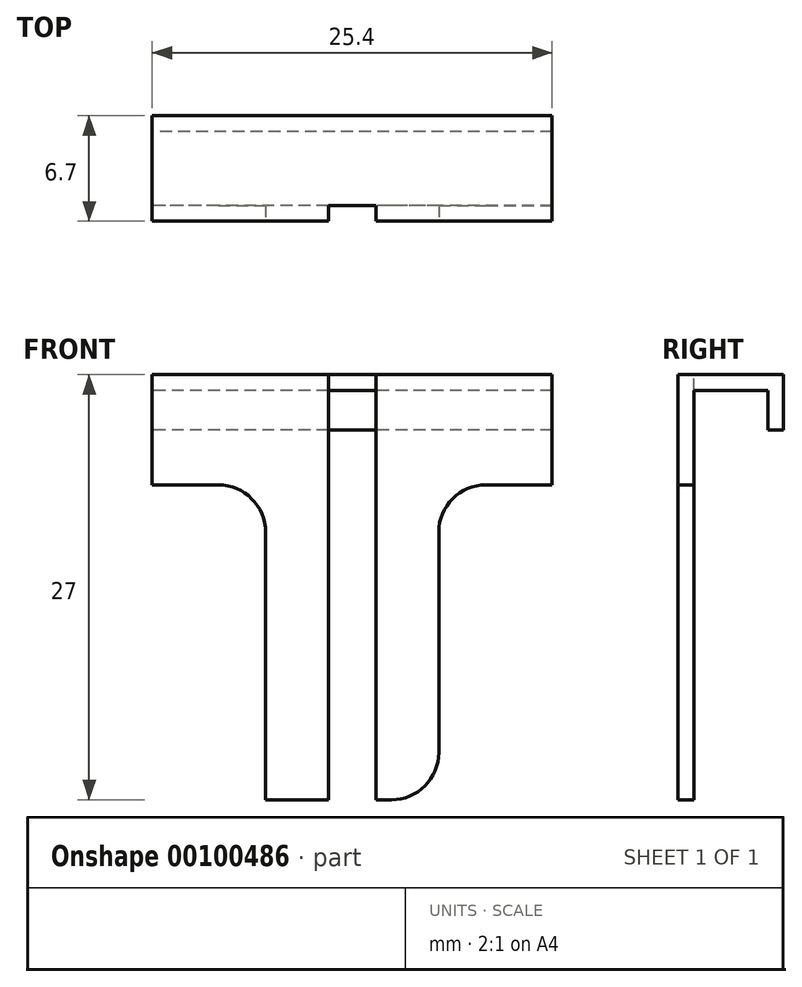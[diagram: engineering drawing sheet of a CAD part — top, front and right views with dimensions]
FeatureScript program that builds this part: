
annotation { "Feature Type Name" : "Feature", "Feature Type Description" : "" }
export const myFeature = defineFeature(function(context is Context, id is Id, definition is map)
    precondition{}
    {
        {
            var Q0;
            Q0=qCreatedBy(makeId("Right.planeOp"),FACE);
            var sketch = newSketch(context, id + "F0", { "sketchPlane" : qUnion([Q0])});
            skLineSegment(sketch, "E0", {"start": v(0, 0) * mm, "end": v(6.7, 0) * mm});
            skLineSegment(sketch, "E1", {"start": v(6.7, 0) * mm, "end": v(6.7, -3.5) * mm});
            skLineSegment(sketch, "E2", {"start": v(6.7, -3.5) * mm, "end": v(5.7, -3.5) * mm});
            skLineSegment(sketch, "E3", {"start": v(5.7, -3.5) * mm, "end": v(5.7, -1) * mm});
            skLineSegment(sketch, "E4", {"start": v(5.7, -1) * mm, "end": v(1, -1) * mm});
            skLineSegment(sketch, "E5", {"start": v(1, -1) * mm, "end": v(1, -27) * mm});
            skLineSegment(sketch, "E6", {"start": v(1, -27) * mm, "end": v(0, -27) * mm});
            skLineSegment(sketch, "E7", {"start": v(0, -27) * mm, "end": v(0, 0) * mm});
            skSolve(sketch);
        }
        {
            var Q0;
            Q0=qSketchRegion(id+"F0",true);
            extrude(context, id + "F1", {"entities" : qUnion([Q0]), "endBound" : BoundingType.SYMMETRIC, "depth" : 25.4 * mm});
        }
        {
            var Q0;
            Q0=makeQuery(id+"F1.opExtrude","SWEPT_FACE",FACE,{"disambiguationData":[OSD([sQuery(id+"F0.wireOp",EDGE,"E7")])]});
            var sketch = newSketch(context, id + "F2", { "sketchPlane" : qUnion([Q0])});
            skLineSegment(sketch, "E8", {"start": v(1.5, 0) * mm, "end": v(-1.5, 0) * mm});
            skLineSegment(sketch, "E9", {"start": v(-5.5, -27) * mm, "end": v(-5.5, -7) * mm});
            skLineSegment(sketch, "E10", {"start": v(5.5, -27) * mm, "end": v(5.5, -7) * mm});
            skLineSegment(sketch, "E11", {"start": v(5.5, -7) * mm, "end": v(12.7, -7) * mm});
            skLineSegment(sketch, "E12", {"start": v(-5.5, -7) * mm, "end": v(-12.7, -7) * mm});
            skLineSegment(sketch, "E13", {"start": v(-12.7, -7) * mm, "end": v(-12.7, -27) * mm});
            skLineSegment(sketch, "E14", {"start": v(-12.7, -27) * mm, "end": v(-5.5, -27) * mm});
            skLineSegment(sketch, "E15", {"start": v(5.5, -27) * mm, "end": v(12.7, -27) * mm});
            skLineSegment(sketch, "E16", {"start": v(12.7, -27) * mm, "end": v(12.7, -7) * mm});
            skLineSegment(sketch, "E17", {"start": v(1.5, -27) * mm, "end": v(1.5, 0) * mm});
            skLineSegment(sketch, "E18", {"start": v(-1.5, -27) * mm, "end": v(-1.5, 0) * mm});
            skLineSegment(sketch, "E19", {"start": v(-1.5, -27) * mm, "end": v(1.5, -27) * mm});
            skSolve(sketch);
        }
        {
            var Q0;
            Q0=qSketchRegion(id+"F2",true);
            var Q1;
            Q1=makeQuery(id+"F1.opExtrude","SWEPT_FACE",FACE,{"disambiguationData":[OSD([sQuery(id+"F0.wireOp",EDGE,"E5")])]});
            extrude(context, id + "F3", {"entities" : qUnion([Q0]), "operationType" : NewBodyOperationType.REMOVE, "endBound" : BoundingType.UP_TO_SURFACE, "oppositeDirection" : true, "endBoundEntityFace" : qUnion([Q1]), "depth" : 25 * mm});
        }
        {
            var Q0;
            Q0=makeQuery(id+"F3.boolean.opBoolean","COPY",EDGE,{"derivedFrom":makeQuery(id+"F3.opExtrude","SWEPT_EDGE",EDGE,{"disambiguationData":[OSD([sQuery(id+"F0.wireOp",EDGE,"E6"),sQuery(id+"F0.wireOp",EDGE,"E7"),sQuery(id+"F2.wireOp",EDGE,"E10"),sQuery(id+"F2.wireOp",EDGE,"E15")])]})});
            var Q1;
            Q1=makeQuery(id+"F3.boolean.opBoolean","COPY",EDGE,{"derivedFrom":makeQuery(id+"F3.opExtrude","SWEPT_EDGE",EDGE,{"disambiguationData":[OSD([sQuery(id+"F0.wireOp",EDGE,"E6"),sQuery(id+"F0.wireOp",EDGE,"E7"),sQuery(id+"F2.wireOp",EDGE,"E9"),sQuery(id+"F2.wireOp",EDGE,"E14")])]})});
            var Q2;
            Q2=makeQuery(id+"F3.boolean.opBoolean","COPY",EDGE,{"derivedFrom":makeQuery(id+"F3.opExtrude","SWEPT_EDGE",EDGE,{"disambiguationData":[OSD([sQuery(id+"F2.wireOp",EDGE,"E9"),sQuery(id+"F2.wireOp",EDGE,"E12")])]})});
            var Q3;
            Q3=makeQuery(id+"F3.boolean.opBoolean","COPY",EDGE,{"derivedFrom":makeQuery(id+"F3.opExtrude","SWEPT_EDGE",EDGE,{"disambiguationData":[OSD([sQuery(id+"F0.wireOp",EDGE,"E7"),sQuery(id+"F2.wireOp",EDGE,"E12"),sQuery(id+"F2.wireOp",EDGE,"E13")])]})});
            var Q4;
            Q4=makeQuery(id+"F3.boolean.opBoolean","COPY",EDGE,{"derivedFrom":makeQuery(id+"F3.opExtrude","SWEPT_EDGE",EDGE,{"disambiguationData":[OSD([sQuery(id+"F2.wireOp",EDGE,"E10"),sQuery(id+"F2.wireOp",EDGE,"E11")])]})});
            var Q5;
            Q5=makeQuery(id+"F3.boolean.opBoolean","COPY",EDGE,{"derivedFrom":makeQuery(id+"F3.opExtrude","SWEPT_EDGE",EDGE,{"disambiguationData":[OSD([sQuery(id+"F0.wireOp",EDGE,"E7"),sQuery(id+"F2.wireOp",EDGE,"E11"),sQuery(id+"F2.wireOp",EDGE,"E16")])]})});
            fillet(context, id + "F4", {"entities" : qUnion([Q0, Q1, Q2, Q3, Q4, Q5]), "radius" : 3 * mm, "tangentPropagation" : true, "allowEdgeOverflow" : false});
        }
    });
